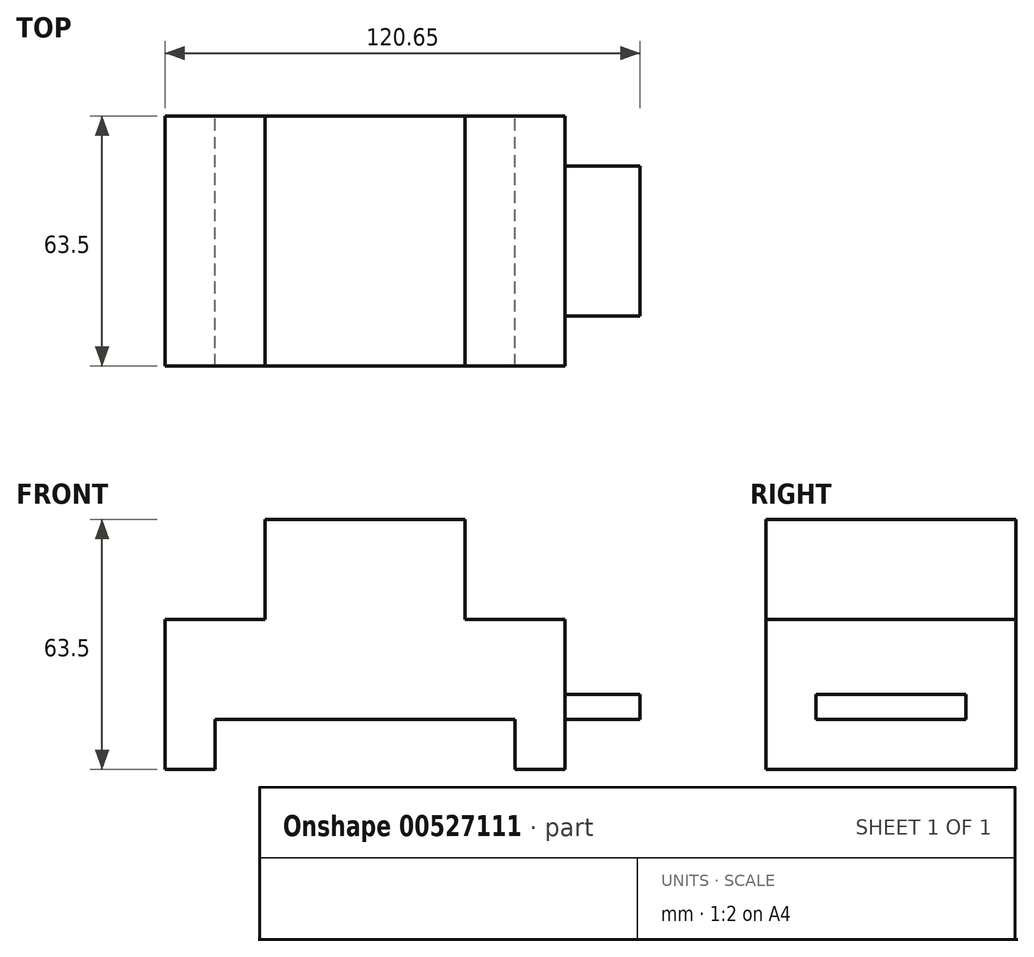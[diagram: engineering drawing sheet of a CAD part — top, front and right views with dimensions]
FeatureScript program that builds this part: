
annotation { "Feature Type Name" : "Feature", "Feature Type Description" : "" }
export const myFeature = defineFeature(function(context is Context, id is Id, definition is map)
    precondition{}
    {
        {
            var Q0;
            Q0=qCreatedBy(makeId("Front.planeOp"),FACE);
            var sketch = newSketch(context, id + "F0", { "sketchPlane" : qUnion([Q0])});
            skLineSegment(sketch, "E0", {"start": v(-61.19, -29.86) * mm, "end": v(-61.19, 8.24) * mm});
            skLineSegment(sketch, "E1", {"start": v(-61.19, 8.24) * mm, "end": v(-35.79, 8.24) * mm});
            skLineSegment(sketch, "E2", {"start": v(-35.79, 8.24) * mm, "end": v(-35.79, 33.64) * mm});
            skLineSegment(sketch, "E3", {"start": v(-35.79, 33.64) * mm, "end": v(15.01, 33.64) * mm});
            skLineSegment(sketch, "E4", {"start": v(15.01, 33.64) * mm, "end": v(15.01, 8.24) * mm});
            skLineSegment(sketch, "E5", {"start": v(15.01, 8.24) * mm, "end": v(40.41, 8.24) * mm});
            skLineSegment(sketch, "E6", {"start": v(-48.49, -29.86) * mm, "end": v(-48.49, -17.16) * mm});
            skLineSegment(sketch, "E7", {"start": v(-48.49, -17.16) * mm, "end": v(27.71, -17.16) * mm});
            skLineSegment(sketch, "E8", {"start": v(27.71, -17.16) * mm, "end": v(27.71, -29.86) * mm});
            skLineSegment(sketch, "E9", {"start": v(-61.19, -29.86) * mm, "end": v(-48.49, -29.86) * mm});
            skLineSegment(sketch, "E10", {"start": v(27.71, -29.86) * mm, "end": v(40.41, -29.86) * mm});
            skLineSegment(sketch, "E11", {"start": v(40.41, -10.8) * mm, "end": v(59.46, -10.8) * mm});
            skLineSegment(sketch, "E12", {"start": v(59.46, -10.8) * mm, "end": v(59.46, -17.16) * mm});
            skLineSegment(sketch, "E13", {"start": v(59.46, -17.16) * mm, "end": v(40.41, -17.16) * mm});
            skLineSegment(sketch, "E14", {"start": v(40.41, 8.24) * mm, "end": v(40.41, -10.8) * mm});
            skLineSegment(sketch, "E15", {"start": v(40.41, -17.16) * mm, "end": v(40.41, -10.8) * mm});
            skLineSegment(sketch, "E16", {"start": v(40.41, -17.16) * mm, "end": v(40.41, -29.86) * mm});
            skSolve(sketch);
        }
        {
            var Q0;
            Q0=makeQuery(id+"F0.imprint","IMPRINT",FACE,{"disambiguationData":[TD([[makeQuery(id+"F0.imprint","IMPRINT",EDGE,{"derivedFrom":sQuery(id+"F0.wireOp",EDGE,"E0")}),-1.0]])]});
            extrude(context, id + "F1", {"entities" : qUnion([Q0]), "endBound" : BoundingType.SYMMETRIC, "depth" : 63.5 * mm});
        }
        {
            var Q0;
            Q0=qSketchRegion(id+"F0",true);
            extrude(context, id + "F2", {"entities" : qUnion([Q0]), "operationType" : NewBodyOperationType.ADD, "endBound" : BoundingType.SYMMETRIC, "depth" : 38.1 * mm});
        }
    });
